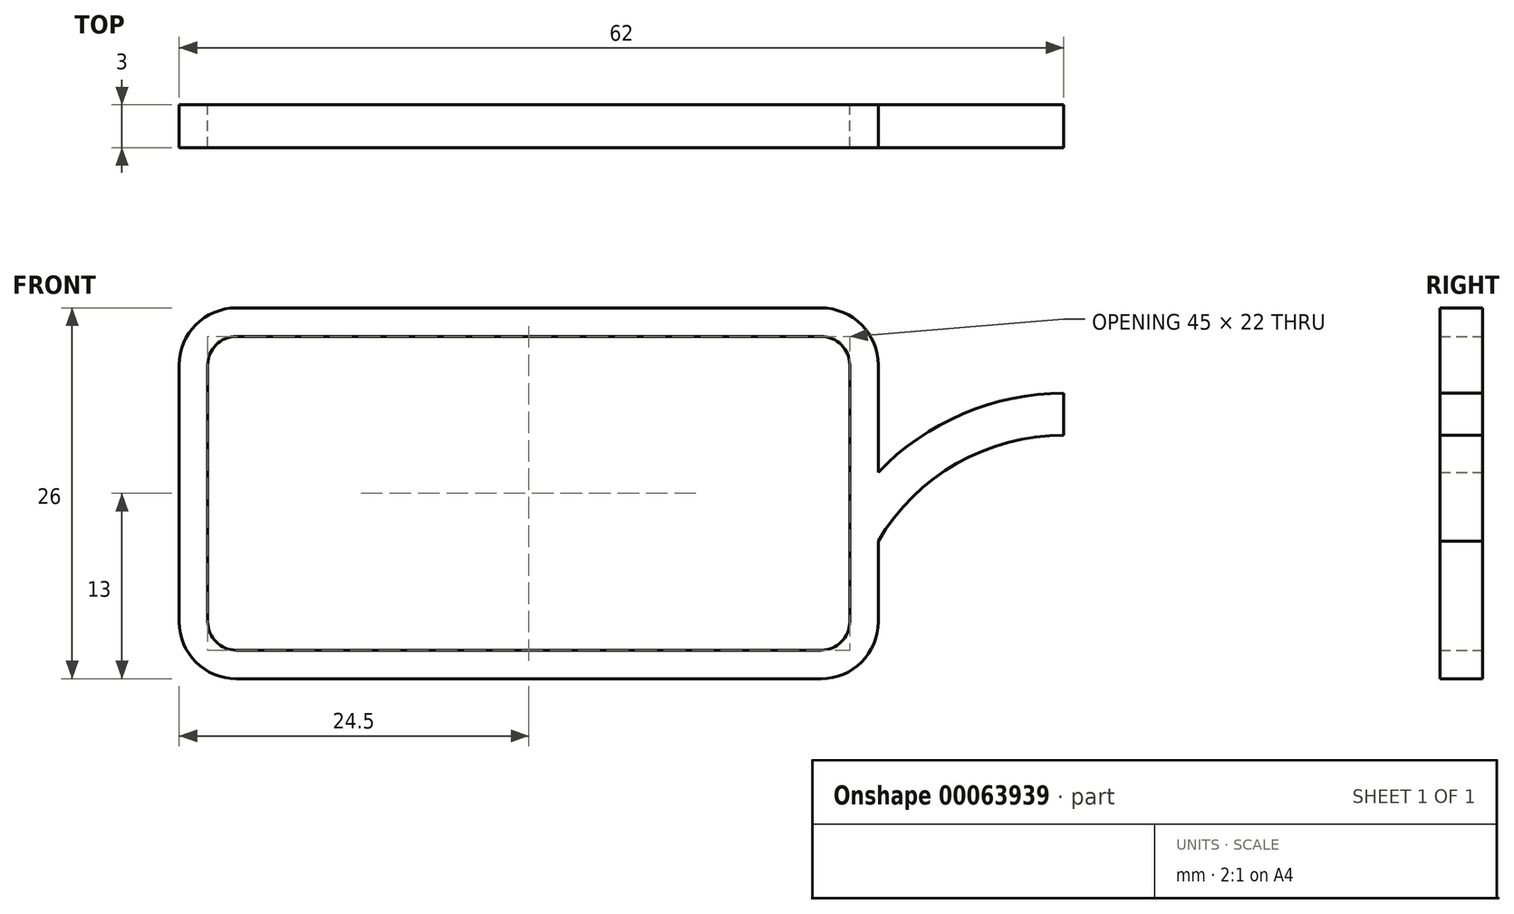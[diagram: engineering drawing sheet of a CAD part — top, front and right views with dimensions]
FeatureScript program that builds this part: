
annotation { "Feature Type Name" : "Feature", "Feature Type Description" : "" }
export const myFeature = defineFeature(function(context is Context, id is Id, definition is map)
    precondition{}
    {
        {
            var Q0;
            Q0=qCreatedBy(makeId("Front.planeOp"),FACE);
            var sketch = newSketch(context, id + "F0", { "sketchPlane" : qUnion([Q0])});
            skLineSegment(sketch, "E0.bottom", {"start": v(-58, 0) * mm, "end": v(-17, 0) * mm});
            skLineSegment(sketch, "E0.top", {"start": v(-58, 22) * mm, "end": v(-17, 22) * mm});
            skLineSegment(sketch, "E0.left", {"start": v(-60, 2) * mm, "end": v(-60, 20) * mm});
            skLineSegment(sketch, "E0.right", {"start": v(-15, 2) * mm, "end": v(-15, 20) * mm});
            skPoint(sketch, "E1.visualSharp", {"position": v(-15, 22) * mm});
            skArc(sketch, "E1.filletArc", {"start": v(-15, 20) * mm, "mid": v(-15.59, 21.41) * mm, "end": v(-17, 22) * mm});
            skPoint(sketch, "E2.visualSharp", {"position": v(-60, 22) * mm});
            skArc(sketch, "E2.filletArc", {"start": v(-58, 22) * mm, "mid": v(-59.41, 21.41) * mm, "end": v(-60, 20) * mm});
            skPoint(sketch, "E3.visualSharp", {"position": v(-60, 0) * mm});
            skArc(sketch, "E3.filletArc", {"start": v(-60, 2) * mm, "mid": v(-59.41, 0.59) * mm, "end": v(-58, 0) * mm});
            skPoint(sketch, "E4.visualSharp", {"position": v(-15, 0) * mm});
            skArc(sketch, "E4.filletArc", {"start": v(-17, 0) * mm, "mid": v(-15.59, 0.59) * mm, "end": v(-15, 2) * mm});
            skArc(sketch, "E5.0", {"start": v(-58, 24) * mm, "mid": v(-60.83, 22.83) * mm, "end": v(-62, 20) * mm});
            skLineSegment(sketch, "E5.1", {"start": v(-62, 2) * mm, "end": v(-62, 20) * mm});
            skLineSegment(sketch, "E5.2", {"start": v(-58, 24) * mm, "end": v(-17, 24) * mm});
            skArc(sketch, "E5.3", {"start": v(-62, 2) * mm, "mid": v(-60.83, -0.83) * mm, "end": v(-58, -2) * mm});
            skArc(sketch, "E5.4", {"start": v(-13, 20) * mm, "mid": v(-14.17, 22.83) * mm, "end": v(-17, 24) * mm});
            skLineSegment(sketch, "E5.5", {"start": v(-13, 2) * mm, "end": v(-13, 7.64) * mm});
            skArc(sketch, "E5.6", {"start": v(-17, -2) * mm, "mid": v(-14.17, -0.83) * mm, "end": v(-13, 2) * mm});
            skLineSegment(sketch, "E5.7", {"start": v(-58, -2) * mm, "end": v(-17, -2) * mm});
            skArc(sketch, "E6", {"start": v(0, 15.08) * mm, "mid": v(-7.49, 13.09) * mm, "end": v(-13, 7.64) * mm});
            skArc(sketch, "E7", {"start": v(0, 18.02) * mm, "mid": v(-7.07, 16.57) * mm, "end": v(-13, 12.47) * mm});
            skLineSegment(sketch, "E8", {"start": v(0, 15.08) * mm, "end": v(0, 18.02) * mm});
            skLineSegment(sketch, "E9.trimOffspring", {"start": v(-13, 12.47) * mm, "end": v(-13, 20) * mm});
            skSolve(sketch);
        }
        {
            var Q0;
            Q0=makeQuery(id+"F0.imprint","IMPRINT",FACE,{"disambiguationData":[TD([[makeQuery(id+"F0.imprint","IMPRINT",EDGE,{"derivedFrom":sQuery(id+"F0.wireOp",EDGE,"E0.bottom")}),-1.0]])]});
            extrude(context, id + "F1", {"entities" : qUnion([Q0]), "depth" : 3 * mm});
        }
    });
